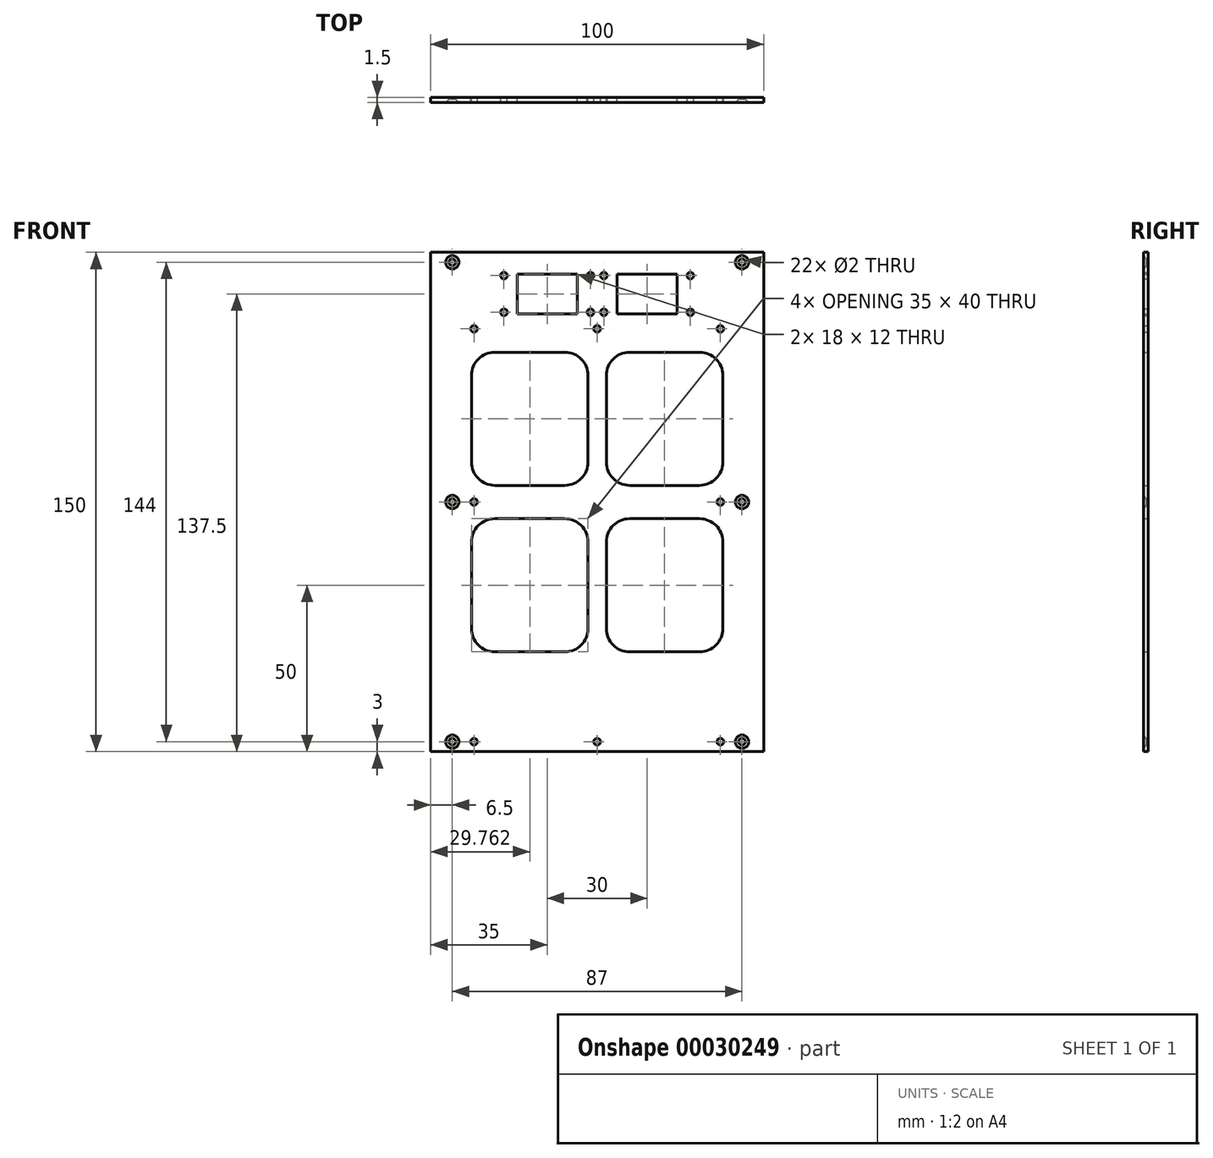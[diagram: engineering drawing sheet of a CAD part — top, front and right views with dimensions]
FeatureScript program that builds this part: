
annotation { "Feature Type Name" : "Feature", "Feature Type Description" : "" }
export const myFeature = defineFeature(function(context is Context, id is Id, definition is map)
    precondition{}
    {
        {
            var Q0;
            Q0=qCreatedBy(makeId("Front.planeOp"),FACE);
            var sketch = newSketch(context, id + "F0", { "sketchPlane" : qUnion([Q0])});
            skLineSegment(sketch, "E0.rect.bottom", {"start": v(-50, 75) * mm, "end": v(50, 75) * mm});
            skLineSegment(sketch, "E0.rect.top", {"start": v(-50, -75) * mm, "end": v(50, -75) * mm});
            skLineSegment(sketch, "E0.rect.left", {"start": v(-50, 75) * mm, "end": v(-50, -75) * mm});
            skLineSegment(sketch, "E0.rect.right", {"start": v(50, 75) * mm, "end": v(50, -75) * mm});
            skPoint(sketch, "E0.rect.middle", {"position": v(0, 0) * mm});
            skLineSegment(sketch, "E1.rect.bottom", {"start": v(-9.74, 5) * mm, "end": v(-30.74, 5) * mm});
            skLineSegment(sketch, "E1.rect.top", {"start": v(-9.74, 45) * mm, "end": v(-30.74, 45) * mm});
            skLineSegment(sketch, "E1.rect.left", {"start": v(-2.74, 12) * mm, "end": v(-2.74, 38) * mm});
            skLineSegment(sketch, "E1.rect.right", {"start": v(-37.74, 12) * mm, "end": v(-37.74, 38) * mm});
            skPoint(sketch, "E1.rect.middle", {"position": v(-20.24, 25) * mm});
            skPoint(sketch, "E2", {"position": v(0, 75) * mm});
            skPoint(sketch, "E3", {"position": v(-25, 75) * mm});
            skPoint(sketch, "E4.visualSharp", {"position": v(-2.74, 5) * mm});
            skArc(sketch, "E4.filletArc", {"start": v(-9.74, 5) * mm, "mid": v(-4.79, 7.05) * mm, "end": v(-2.74, 12) * mm});
            skPoint(sketch, "E5.visualSharp", {"position": v(-2.74, 45) * mm});
            skArc(sketch, "E5.filletArc", {"start": v(-2.74, 38) * mm, "mid": v(-4.79, 42.95) * mm, "end": v(-9.74, 45) * mm});
            skPoint(sketch, "E6.visualSharp", {"position": v(-37.74, 45) * mm});
            skArc(sketch, "E6.filletArc", {"start": v(-30.74, 45) * mm, "mid": v(-35.69, 42.95) * mm, "end": v(-37.74, 38) * mm});
            skPoint(sketch, "E7.visualSharp", {"position": v(-37.74, 5) * mm});
            skArc(sketch, "E7.filletArc", {"start": v(-37.74, 12) * mm, "mid": v(-35.69, 7.05) * mm, "end": v(-30.74, 5) * mm});
            skLineSegment(sketch, "E8.MirrorCS", {"start": v(2.74, 12) * mm, "end": v(2.74, 38) * mm});
            skArc(sketch, "E9.MirrorCS", {"start": v(2.74, 38) * mm, "mid": v(4.79, 42.95) * mm, "end": v(9.74, 45) * mm});
            skLineSegment(sketch, "E10.MirrorCS", {"start": v(9.74, 45) * mm, "end": v(30.74, 45) * mm});
            skPoint(sketch, "E11.MirrorP", {"position": v(37.74, 45) * mm});
            skArc(sketch, "E12.MirrorCS", {"start": v(30.74, 45) * mm, "mid": v(35.69, 42.95) * mm, "end": v(37.74, 38) * mm});
            skLineSegment(sketch, "E13.MirrorCS", {"start": v(37.74, 12) * mm, "end": v(37.74, 38) * mm});
            skPoint(sketch, "E14.MirrorP", {"position": v(37.74, 5) * mm});
            skLineSegment(sketch, "E15.MirrorCS", {"start": v(9.74, 5) * mm, "end": v(30.74, 5) * mm});
            skArc(sketch, "E16.MirrorCS", {"start": v(37.74, 12) * mm, "mid": v(35.69, 7.05) * mm, "end": v(30.74, 5) * mm});
            skPoint(sketch, "E17.MirrorP", {"position": v(2.74, 5) * mm});
            skArc(sketch, "E18.MirrorCS", {"start": v(9.74, 5) * mm, "mid": v(4.79, 7.05) * mm, "end": v(2.74, 12) * mm});
            skArc(sketch, "E19.MirrorCS", {"start": v(30.74, -45) * mm, "mid": v(35.69, -42.95) * mm, "end": v(37.74, -38) * mm});
            skArc(sketch, "E20.MirrorCS", {"start": v(37.74, -12) * mm, "mid": v(35.69, -7.05) * mm, "end": v(30.74, -5) * mm});
            skArc(sketch, "E21.MirrorCS", {"start": v(9.74, -5) * mm, "mid": v(4.79, -7.05) * mm, "end": v(2.74, -12) * mm});
            skArc(sketch, "E22.MirrorCS", {"start": v(2.74, -38) * mm, "mid": v(4.79, -42.95) * mm, "end": v(9.74, -45) * mm});
            skPoint(sketch, "E23.MirrorP", {"position": v(37.74, -45) * mm});
            skLineSegment(sketch, "E24.MirrorCS", {"start": v(37.74, -12) * mm, "end": v(37.74, -38) * mm});
            skPoint(sketch, "E25.MirrorP", {"position": v(37.74, -5) * mm});
            skLineSegment(sketch, "E26.MirrorCS", {"start": v(2.74, -12) * mm, "end": v(2.74, -38) * mm});
            skPoint(sketch, "E27.MirrorP", {"position": v(3.64, -53) * mm});
            skLineSegment(sketch, "E28.MirrorCS", {"start": v(9.74, -5) * mm, "end": v(30.74, -5) * mm});
            skLineSegment(sketch, "E29.MirrorCS", {"start": v(9.74, -45) * mm, "end": v(30.74, -45) * mm});
            skPoint(sketch, "E30.MirrorP", {"position": v(2.74, -5) * mm});
            skArc(sketch, "E31.MirrorCS", {"start": v(-9.74, -5) * mm, "mid": v(-4.79, -7.05) * mm, "end": v(-2.74, -12) * mm});
            skArc(sketch, "E32.MirrorCS", {"start": v(-2.74, -38) * mm, "mid": v(-4.79, -42.95) * mm, "end": v(-9.74, -45) * mm});
            skArc(sketch, "E33.MirrorCS", {"start": v(-37.74, -12) * mm, "mid": v(-35.69, -7.05) * mm, "end": v(-30.74, -5) * mm});
            skArc(sketch, "E34.MirrorCS", {"start": v(-30.74, -45) * mm, "mid": v(-35.69, -42.95) * mm, "end": v(-37.74, -38) * mm});
            skPoint(sketch, "E35.MirrorP", {"position": v(-20.24, -25) * mm});
            skPoint(sketch, "E36.MirrorP", {"position": v(-2.74, -5) * mm});
            skPoint(sketch, "E37.MirrorP", {"position": v(-37.74, -45) * mm});
            skLineSegment(sketch, "E38.MirrorCS", {"start": v(-9.74, -5) * mm, "end": v(-30.74, -5) * mm});
            skLineSegment(sketch, "E39.MirrorCS", {"start": v(-9.74, -45) * mm, "end": v(-30.74, -45) * mm});
            skPoint(sketch, "E40.MirrorP", {"position": v(-2.74, -45) * mm});
            skLineSegment(sketch, "E41.MirrorCS", {"start": v(-2.74, -12) * mm, "end": v(-2.74, -38) * mm});
            skLineSegment(sketch, "E42.MirrorCS", {"start": v(-37.74, -12) * mm, "end": v(-37.74, -38) * mm});
            skPoint(sketch, "E43.MirrorP", {"position": v(-37.74, -5) * mm});
            skLineSegment(sketch, "E44.bottom", {"start": v(-24, 68.5) * mm, "end": v(-6, 68.5) * mm});
            skLineSegment(sketch, "E44.top", {"start": v(-24, 56.5) * mm, "end": v(-6, 56.5) * mm});
            skLineSegment(sketch, "E44.left", {"start": v(-24, 68.5) * mm, "end": v(-24, 56.5) * mm});
            skLineSegment(sketch, "E44.right", {"start": v(-6, 68.5) * mm, "end": v(-6, 56.5) * mm});
            skPoint(sketch, "E45", {"position": v(-28, 57) * mm});
            skPoint(sketch, "E46", {"position": v(-28, 68) * mm});
            skPoint(sketch, "E47", {"position": v(-15, 68.5) * mm});
            skPoint(sketch, "E48", {"position": v(-15, 56.5) * mm});
            skLineSegment(sketch, "E49", {"start": v(-15, 68.5) * mm, "end": v(-15, 56.5) * mm});
            skPoint(sketch, "E50.MirrorP", {"position": v(-2, 68) * mm});
            skPoint(sketch, "E51.MirrorP", {"position": v(-2, 57) * mm});
            skPoint(sketch, "E52.MirrorP", {"position": v(2, 68) * mm});
            skPoint(sketch, "E53.MirrorP", {"position": v(28, 57) * mm});
            skPoint(sketch, "E54.MirrorP", {"position": v(2, 57) * mm});
            skLineSegment(sketch, "E55.MirrorCS", {"start": v(6, 68.5) * mm, "end": v(6, 56.5) * mm});
            skLineSegment(sketch, "E56.MirrorCS", {"start": v(24, 68.5) * mm, "end": v(6, 68.5) * mm});
            skLineSegment(sketch, "E57.MirrorCS", {"start": v(24, 68.5) * mm, "end": v(24, 56.5) * mm});
            skLineSegment(sketch, "E58.MirrorCS", {"start": v(15, 68.5) * mm, "end": v(15, 56.5) * mm});
            skPoint(sketch, "E59.MirrorP", {"position": v(15, 68.5) * mm});
            skPoint(sketch, "E60.MirrorP", {"position": v(28, 68) * mm});
            skLineSegment(sketch, "E61.MirrorCS", {"start": v(24, 56.5) * mm, "end": v(6, 56.5) * mm});
            skPoint(sketch, "E62.MirrorP", {"position": v(2.74, 45) * mm});
            skPoint(sketch, "E63.MirrorP", {"position": v(15, 56.5) * mm});
            skPoint(sketch, "E64", {"position": v(0, -75) * mm});
            skSolve(sketch);
        }
        {
            var Q0;
            Q0=makeQuery(id+"F0.imprint","IMPRINT",FACE,{"disambiguationData":[TD([[makeQuery(id+"F0.imprint","IMPRINT",EDGE,{"derivedFrom":sQuery(id+"F0.wireOp",EDGE,"E0.rect.bottom")}),-1.0]])]});
            extrude(context, id + "F1", {"entities" : qUnion([Q0]), "depth" : 1.5 * mm});
        }
        {
            var Q0;
            Q0=makeQuery(id+"F1.opExtrude","CAP_FACE",FACE,{"disambiguationData":[OSD([sQuery(id+"F0.wireOp",EDGE,"E0.rect.bottom"),sQuery(id+"F0.wireOp",EDGE,"E0.rect.top"),sQuery(id+"F0.wireOp",EDGE,"E0.rect.left"),sQuery(id+"F0.wireOp",EDGE,"E0.rect.right"),sQuery(id+"F0.wireOp",EDGE,"E1.rect.bottom"),sQuery(id+"F0.wireOp",EDGE,"E1.rect.top"),sQuery(id+"F0.wireOp",EDGE,"E1.rect.left"),sQuery(id+"F0.wireOp",EDGE,"E1.rect.right"),sQuery(id+"F0.wireOp",EDGE,"E4.filletArc"),sQuery(id+"F0.wireOp",EDGE,"E5.filletArc"),sQuery(id+"F0.wireOp",EDGE,"E6.filletArc"),sQuery(id+"F0.wireOp",EDGE,"E7.filletArc"),sQuery(id+"F0.wireOp",EDGE,"E8.MirrorCS"),sQuery(id+"F0.wireOp",EDGE,"E9.MirrorCS"),sQuery(id+"F0.wireOp",EDGE,"E10.MirrorCS"),sQuery(id+"F0.wireOp",EDGE,"E12.MirrorCS"),sQuery(id+"F0.wireOp",EDGE,"E13.MirrorCS"),sQuery(id+"F0.wireOp",EDGE,"E15.MirrorCS"),sQuery(id+"F0.wireOp",EDGE,"E16.MirrorCS"),sQuery(id+"F0.wireOp",EDGE,"E18.MirrorCS"),sQuery(id+"F0.wireOp",EDGE,"E19.MirrorCS"),sQuery(id+"F0.wireOp",EDGE,"E20.MirrorCS"),sQuery(id+"F0.wireOp",EDGE,"E21.MirrorCS"),sQuery(id+"F0.wireOp",EDGE,"E22.MirrorCS"),sQuery(id+"F0.wireOp",EDGE,"E24.MirrorCS"),sQuery(id+"F0.wireOp",EDGE,"E26.MirrorCS"),sQuery(id+"F0.wireOp",EDGE,"E28.MirrorCS"),sQuery(id+"F0.wireOp",EDGE,"E29.MirrorCS"),sQuery(id+"F0.wireOp",EDGE,"E31.MirrorCS"),sQuery(id+"F0.wireOp",EDGE,"E32.MirrorCS"),sQuery(id+"F0.wireOp",EDGE,"E33.MirrorCS"),sQuery(id+"F0.wireOp",EDGE,"E34.MirrorCS"),sQuery(id+"F0.wireOp",EDGE,"E38.MirrorCS"),sQuery(id+"F0.wireOp",EDGE,"E39.MirrorCS"),sQuery(id+"F0.wireOp",EDGE,"E41.MirrorCS"),sQuery(id+"F0.wireOp",EDGE,"E42.MirrorCS"),sQuery(id+"F0.wireOp",EDGE,"deea28ce-c4f6-4fc3-8f0f-82602a925565.rect.bottom"),sQuery(id+"F0.wireOp",EDGE,"deea28ce-c4f6-4fc3-8f0f-82602a925565.rect.top"),sQuery(id+"F0.wireOp",EDGE,"deea28ce-c4f6-4fc3-8f0f-82602a925565.rect.left"),sQuery(id+"F0.wireOp",EDGE,"deea28ce-c4f6-4fc3-8f0f-82602a925565.rect.right"),sQuery(id+"F0.wireOp",EDGE,"92293470-82ba-44ad-9286-e8a1911384cd.filletArc"),sQuery(id+"F0.wireOp",EDGE,"f783d059-47c1-4597-a3b5-ce5ed20d1783.filletArc"),sQuery(id+"F0.wireOp",EDGE,"7d8a2005-66fb-4448-9a0b-17e6f11710ed.filletArc"),sQuery(id+"F0.wireOp",EDGE,"bd1f88c4-01d0-4c1f-b818-689555ed0d3d.filletArc"),sQuery(id+"F0.wireOp",EDGE,"3de75153-5ae1-45d4-89d9-6fcf70203f930.MirrorCS"),sQuery(id+"F0.wireOp",EDGE,"3de75153-5ae1-45d4-89d9-6fcf70203f931.MirrorCS"),sQuery(id+"F0.wireOp",EDGE,"3de75153-5ae1-45d4-89d9-6fcf70203f932.MirrorCS"),sQuery(id+"F0.wireOp",EDGE,"3de75153-5ae1-45d4-89d9-6fcf70203f933.MirrorCS"),sQuery(id+"F0.wireOp",EDGE,"3de75153-5ae1-45d4-89d9-6fcf70203f937.MirrorCS"),sQuery(id+"F0.wireOp",EDGE,"3de75153-5ae1-45d4-89d9-6fcf70203f939.MirrorCS"),sQuery(id+"F0.wireOp",EDGE,"3de75153-5ae1-45d4-89d9-6fcf70203f9311.MirrorCS"),sQuery(id+"F0.wireOp",EDGE,"3de75153-5ae1-45d4-89d9-6fcf70203f9312.MirrorCS")])],"isStart":false});
            var sketch = newSketch(context, id + "F2", { "sketchPlane" : qUnion([Q0])});
            skPoint(sketch, "E65", {"position": v(-43.5, -72) * mm});
            skPoint(sketch, "E66.MirrorP", {"position": v(43.5, -72) * mm});
            skPoint(sketch, "E67.MirrorP", {"position": v(-43.5, 72) * mm});
            skPoint(sketch, "E68.MirrorP", {"position": v(43.5, 72) * mm});
            skPoint(sketch, "E69.MirrorP", {"position": v(-43.5, 0) * mm});
            skPoint(sketch, "E70.MirrorP", {"position": v(43.5, 0) * mm});
            skSolve(sketch);
        }
        {
            var Q0;
            Q0=sQuery(id+"F2.wireOp",VERTEX,"E65");
            var Q1;
            Q1=sQuery(id+"F2.wireOp",VERTEX,"E66.MirrorP");
            var Q2;
            Q2=sQuery(id+"F2.wireOp",VERTEX,"E68.MirrorP");
            var Q3;
            Q3=sQuery(id+"F2.wireOp",VERTEX,"E67.MirrorP");
            var Q4;
            Q4=sQuery(id+"F2.wireOp",VERTEX,"f692f96d-b3ef-4b25-bd05-95c4abe1053b");
            var Q5;
            Q5=sQuery(id+"F2.wireOp",VERTEX,"6fb1c37c-decf-44f5-8bba-7a2e60b1c09a");
            var Q6;
            Q6=sQuery(id+"F2.wireOp",VERTEX,"e5432b45-bd6c-42e0-96c4-d4a1cdefc3be");
            var Q7;
            Q7=sQuery(id+"F2.wireOp",VERTEX,"cf76a1ca-a373-4096-b586-4708a9325641");
            var Q8;
            Q8=sQuery(id+"F2.wireOp",VERTEX,"19e9ac87-c4db-4f84-8793-d0dcfe6b89480.MirrorP");
            var Q9;
            Q9=sQuery(id+"F2.wireOp",VERTEX,"cf40c92d-3cb4-4fd1-9011-2b1b11cf86800.MirrorP");
            var Q10;
            Q10=sQuery(id+"F2.wireOp",VERTEX,"dbe2afd2-cc13-4726-9d4e-a7426feb8f1a0.MirrorP");
            var Q11;
            Q11=sQuery(id+"F2.wireOp",VERTEX,"da7565b5-0760-4871-9ab9-0602c46f39720.MirrorP");
            var Q12;
            Q12=sQuery(id+"F2.wireOp",VERTEX,"17fecccd-3962-452f-9978-7328e825eee30.MirrorP");
            var Q13;
            Q13=sQuery(id+"F2.wireOp",VERTEX,"4bd07c42-14cb-4c0a-9484-79320a5c3db60.MirrorP");
            var Q14;
            Q14=sQuery(id+"F2.wireOp",VERTEX,"4bebc43e-6cee-4dba-a944-25e79cf908630.MirrorP");
            var Q15;
            Q15=sQuery(id+"F2.wireOp",VERTEX,"e56d2771-9223-44ee-8796-3a5c91e851be0.MirrorP");
            var Q16;
            Q16=sQuery(id+"F2.wireOp",VERTEX,"fc323023-5ca8-47af-bc60-2d4e8e6fe2a30.MirrorP");
            var Q17;
            Q17=sQuery(id+"F2.wireOp",VERTEX,"0839c29d-2d7f-409f-b01c-e3268e62f07b0.MirrorP");
            var Q18;
            Q18=sQuery(id+"F2.wireOp",VERTEX,"a23aa490-2248-47f4-872f-093390e742580.MirrorP");
            var Q19;
            Q19=sQuery(id+"F2.wireOp",VERTEX,"f29489ae-a8f8-488d-b8ee-71de4e1048c30.MirrorP");
            var Q20;
            Q20=sQuery(id+"F2.wireOp",VERTEX,"E69.MirrorP");
            var Q21;
            Q21=sQuery(id+"F2.wireOp",VERTEX,"E70.MirrorP");
            var Q22;
            Q22=makeQuery(id+"F1.opExtrude","SWEPT_BODY",BODY,{"disambiguationData":[OSD([sQuery(id+"F0.wireOp",EDGE,"E0.rect.bottom"),sQuery(id+"F0.wireOp",EDGE,"E0.rect.top"),sQuery(id+"F0.wireOp",EDGE,"E0.rect.left"),sQuery(id+"F0.wireOp",EDGE,"E0.rect.right"),sQuery(id+"F0.wireOp",EDGE,"E1.rect.bottom"),sQuery(id+"F0.wireOp",EDGE,"E1.rect.top"),sQuery(id+"F0.wireOp",EDGE,"E1.rect.left"),sQuery(id+"F0.wireOp",EDGE,"E1.rect.right"),sQuery(id+"F0.wireOp",EDGE,"E4.filletArc"),sQuery(id+"F0.wireOp",EDGE,"E5.filletArc"),sQuery(id+"F0.wireOp",EDGE,"E6.filletArc"),sQuery(id+"F0.wireOp",EDGE,"E7.filletArc"),sQuery(id+"F0.wireOp",EDGE,"E8.MirrorCS"),sQuery(id+"F0.wireOp",EDGE,"E9.MirrorCS"),sQuery(id+"F0.wireOp",EDGE,"E10.MirrorCS"),sQuery(id+"F0.wireOp",EDGE,"E12.MirrorCS"),sQuery(id+"F0.wireOp",EDGE,"E13.MirrorCS"),sQuery(id+"F0.wireOp",EDGE,"E15.MirrorCS"),sQuery(id+"F0.wireOp",EDGE,"E16.MirrorCS"),sQuery(id+"F0.wireOp",EDGE,"E18.MirrorCS"),sQuery(id+"F0.wireOp",EDGE,"E19.MirrorCS"),sQuery(id+"F0.wireOp",EDGE,"E20.MirrorCS"),sQuery(id+"F0.wireOp",EDGE,"E21.MirrorCS"),sQuery(id+"F0.wireOp",EDGE,"E22.MirrorCS"),sQuery(id+"F0.wireOp",EDGE,"E24.MirrorCS"),sQuery(id+"F0.wireOp",EDGE,"E26.MirrorCS"),sQuery(id+"F0.wireOp",EDGE,"E28.MirrorCS"),sQuery(id+"F0.wireOp",EDGE,"E29.MirrorCS"),sQuery(id+"F0.wireOp",EDGE,"E31.MirrorCS"),sQuery(id+"F0.wireOp",EDGE,"E32.MirrorCS"),sQuery(id+"F0.wireOp",EDGE,"E33.MirrorCS"),sQuery(id+"F0.wireOp",EDGE,"E34.MirrorCS"),sQuery(id+"F0.wireOp",EDGE,"E38.MirrorCS"),sQuery(id+"F0.wireOp",EDGE,"E39.MirrorCS"),sQuery(id+"F0.wireOp",EDGE,"E41.MirrorCS"),sQuery(id+"F0.wireOp",EDGE,"E42.MirrorCS"),sQuery(id+"F0.wireOp",EDGE,"deea28ce-c4f6-4fc3-8f0f-82602a925565.rect.bottom"),sQuery(id+"F0.wireOp",EDGE,"deea28ce-c4f6-4fc3-8f0f-82602a925565.rect.top"),sQuery(id+"F0.wireOp",EDGE,"deea28ce-c4f6-4fc3-8f0f-82602a925565.rect.left"),sQuery(id+"F0.wireOp",EDGE,"deea28ce-c4f6-4fc3-8f0f-82602a925565.rect.right"),sQuery(id+"F0.wireOp",EDGE,"92293470-82ba-44ad-9286-e8a1911384cd.filletArc"),sQuery(id+"F0.wireOp",EDGE,"f783d059-47c1-4597-a3b5-ce5ed20d1783.filletArc"),sQuery(id+"F0.wireOp",EDGE,"7d8a2005-66fb-4448-9a0b-17e6f11710ed.filletArc"),sQuery(id+"F0.wireOp",EDGE,"bd1f88c4-01d0-4c1f-b818-689555ed0d3d.filletArc"),sQuery(id+"F0.wireOp",EDGE,"3de75153-5ae1-45d4-89d9-6fcf70203f930.MirrorCS"),sQuery(id+"F0.wireOp",EDGE,"3de75153-5ae1-45d4-89d9-6fcf70203f931.MirrorCS"),sQuery(id+"F0.wireOp",EDGE,"3de75153-5ae1-45d4-89d9-6fcf70203f932.MirrorCS"),sQuery(id+"F0.wireOp",EDGE,"3de75153-5ae1-45d4-89d9-6fcf70203f933.MirrorCS"),sQuery(id+"F0.wireOp",EDGE,"3de75153-5ae1-45d4-89d9-6fcf70203f937.MirrorCS"),sQuery(id+"F0.wireOp",EDGE,"3de75153-5ae1-45d4-89d9-6fcf70203f939.MirrorCS"),sQuery(id+"F0.wireOp",EDGE,"3de75153-5ae1-45d4-89d9-6fcf70203f9311.MirrorCS"),sQuery(id+"F0.wireOp",EDGE,"3de75153-5ae1-45d4-89d9-6fcf70203f9312.MirrorCS")])]});
            hole(context, id + "F3", {"style" : HoleStyle.C_SINK, "holeDiameter" : 2 * mm, "cSinkDiameter" : 4 * mm, "endStyle" : HoleEndStyle.THROUGH, "locations" : qUnion([Q0, Q1, Q2, Q3, Q4, Q5, Q6, Q7, Q8, Q9, Q10, Q11, Q12, Q13, Q14, Q15, Q16, Q17, Q18, Q19, Q20, Q21]), "scope" : qUnion([Q22]), "cSinkAngle" : 90 * degree, "isTappedThrough" : true});
        }
        {
            var Q0;
            Q0=sQuery(id+"F0.wireOp",VERTEX,"E46");
            var Q1;
            Q1=sQuery(id+"F0.wireOp",VERTEX,"E45");
            var Q2;
            Q2=sQuery(id+"F0.wireOp",VERTEX,"E51.MirrorP");
            var Q3;
            Q3=sQuery(id+"F0.wireOp",VERTEX,"E50.MirrorP");
            var Q4;
            Q4=sQuery(id+"F0.wireOp",VERTEX,"E52.MirrorP");
            var Q5;
            Q5=sQuery(id+"F0.wireOp",VERTEX,"E54.MirrorP");
            var Q6;
            Q6=sQuery(id+"F0.wireOp",VERTEX,"E53.MirrorP");
            var Q7;
            Q7=sQuery(id+"F0.wireOp",VERTEX,"E60.MirrorP");
            var Q8;
            Q8=makeQuery(id+"F1.opExtrude","SWEPT_BODY",BODY,{"disambiguationData":[OSD([sQuery(id+"F0.wireOp",EDGE,"E0.rect.bottom"),sQuery(id+"F0.wireOp",EDGE,"E0.rect.top"),sQuery(id+"F0.wireOp",EDGE,"E0.rect.left"),sQuery(id+"F0.wireOp",EDGE,"E0.rect.right"),sQuery(id+"F0.wireOp",EDGE,"E1.rect.bottom"),sQuery(id+"F0.wireOp",EDGE,"E1.rect.top"),sQuery(id+"F0.wireOp",EDGE,"E1.rect.left"),sQuery(id+"F0.wireOp",EDGE,"E1.rect.right"),sQuery(id+"F0.wireOp",EDGE,"E4.filletArc"),sQuery(id+"F0.wireOp",EDGE,"E5.filletArc"),sQuery(id+"F0.wireOp",EDGE,"E6.filletArc"),sQuery(id+"F0.wireOp",EDGE,"E7.filletArc"),sQuery(id+"F0.wireOp",EDGE,"E8.MirrorCS"),sQuery(id+"F0.wireOp",EDGE,"E9.MirrorCS"),sQuery(id+"F0.wireOp",EDGE,"E10.MirrorCS"),sQuery(id+"F0.wireOp",EDGE,"E12.MirrorCS"),sQuery(id+"F0.wireOp",EDGE,"E13.MirrorCS"),sQuery(id+"F0.wireOp",EDGE,"E15.MirrorCS"),sQuery(id+"F0.wireOp",EDGE,"E16.MirrorCS"),sQuery(id+"F0.wireOp",EDGE,"E18.MirrorCS"),sQuery(id+"F0.wireOp",EDGE,"E19.MirrorCS"),sQuery(id+"F0.wireOp",EDGE,"E20.MirrorCS"),sQuery(id+"F0.wireOp",EDGE,"E21.MirrorCS"),sQuery(id+"F0.wireOp",EDGE,"E22.MirrorCS"),sQuery(id+"F0.wireOp",EDGE,"E24.MirrorCS"),sQuery(id+"F0.wireOp",EDGE,"E26.MirrorCS"),sQuery(id+"F0.wireOp",EDGE,"E28.MirrorCS"),sQuery(id+"F0.wireOp",EDGE,"E29.MirrorCS"),sQuery(id+"F0.wireOp",EDGE,"E31.MirrorCS"),sQuery(id+"F0.wireOp",EDGE,"E32.MirrorCS"),sQuery(id+"F0.wireOp",EDGE,"E33.MirrorCS"),sQuery(id+"F0.wireOp",EDGE,"E34.MirrorCS"),sQuery(id+"F0.wireOp",EDGE,"E38.MirrorCS"),sQuery(id+"F0.wireOp",EDGE,"E39.MirrorCS"),sQuery(id+"F0.wireOp",EDGE,"E41.MirrorCS"),sQuery(id+"F0.wireOp",EDGE,"E42.MirrorCS"),sQuery(id+"F0.wireOp",EDGE,"0ad36b47-e3a2-4d15-89b1-ac590451d19c"),sQuery(id+"F0.wireOp",EDGE,"E44.bottom"),sQuery(id+"F0.wireOp",EDGE,"E44.top"),sQuery(id+"F0.wireOp",EDGE,"E44.left"),sQuery(id+"F0.wireOp",EDGE,"E44.right"),sQuery(id+"F0.wireOp",EDGE,"E55.MirrorCS"),sQuery(id+"F0.wireOp",EDGE,"E56.MirrorCS"),sQuery(id+"F0.wireOp",EDGE,"E57.MirrorCS"),sQuery(id+"F0.wireOp",EDGE,"E61.MirrorCS")])]});
            hole(context, id + "F4", {"style" : HoleStyle.SIMPLE, "endStyle" : HoleEndStyle.THROUGH, "oppositeDirection" : true, "holeDiameter" : 2 * mm, "locations" : qUnion([Q0, Q1, Q2, Q3, Q4, Q5, Q6, Q7]), "scope" : qUnion([Q8]), "isTappedThrough" : true});
        }
        {
            var Q0;
            Q0=qCreatedBy(makeId("Front.planeOp"),FACE);
            var sketch = newSketch(context, id + "F5", { "sketchPlane" : qUnion([Q0])});
            skCircle(sketch, "E71", {"center": v(-37, -72) * mm, "radius": 1 * mm});
            skCircle(sketch, "E72.0.1.0", {"center": v(-37, 52) * mm, "radius": 1 * mm});
            skCircle(sketch, "E72.1.0.0", {"center": v(0, -72) * mm, "radius": 1 * mm});
            skCircle(sketch, "E72.1.1.0", {"center": v(0, 52) * mm, "radius": 1 * mm});
            skCircle(sketch, "E72.2.0.0", {"center": v(37, -72) * mm, "radius": 1 * mm});
            skCircle(sketch, "E72.2.1.0", {"center": v(37, 52) * mm, "radius": 1 * mm});
            skLineSegment(sketch, "E72.direction1", {"start": v(-37, -72) * mm, "end": v(0, -72) * mm, "construction": true});
            skLineSegment(sketch, "E72.direction2", {"start": v(-37, -72) * mm, "end": v(-37, 52) * mm, "construction": true});
            skPoint(sketch, "E73", {"position": v(-37, 0) * mm});
            skPoint(sketch, "E74.MirrorP", {"position": v(37, 0) * mm});
            skSolve(sketch);
        }
        {
            var Q0;
            Q0=sQuery(id+"F5.wireOp",VERTEX,"E72.direction1.start");
            var Q1;
            Q1=sQuery(id+"F5.wireOp",VERTEX,"E72.direction1.end");
            var Q2;
            Q2=sQuery(id+"F5.wireOp",VERTEX,"E72.2.0.0.center");
            var Q3;
            Q3=sQuery(id+"F5.wireOp",VERTEX,"E72.1.1.0.center");
            var Q4;
            Q4=sQuery(id+"F5.wireOp",VERTEX,"E72.1.2.0.center");
            var Q5;
            Q5=sQuery(id+"F5.wireOp",VERTEX,"E72.2.2.0.center");
            var Q6;
            Q6=sQuery(id+"F5.wireOp",VERTEX,"E72.0.2.0.center");
            var Q7;
            Q7=sQuery(id+"F5.wireOp",VERTEX,"E72.direction2.end");
            var Q8;
            Q8=sQuery(id+"F5.wireOp",VERTEX,"E72.2.1.0.center");
            var Q9;
            Q9=sQuery(id+"F5.wireOp",VERTEX,"8d9ffd20-42a7-48bb-b160-9022e51994f8");
            var Q10;
            Q10=sQuery(id+"F5.wireOp",VERTEX,"2204d435-fe16-46ed-8ace-113c7e8db4ec0.MirrorP");
            var Q11;
            Q11=sQuery(id+"F5.wireOp",VERTEX,"E73");
            var Q12;
            Q12=sQuery(id+"F5.wireOp",VERTEX,"E74.MirrorP");
            var Q13;
            Q13=makeQuery(id+"F1.opExtrude","SWEPT_BODY",BODY,{"disambiguationData":[OSD([sQuery(id+"F0.wireOp",EDGE,"E0.rect.bottom"),sQuery(id+"F0.wireOp",EDGE,"E0.rect.top"),sQuery(id+"F0.wireOp",EDGE,"E0.rect.left"),sQuery(id+"F0.wireOp",EDGE,"E0.rect.right"),sQuery(id+"F0.wireOp",EDGE,"E1.rect.bottom"),sQuery(id+"F0.wireOp",EDGE,"E1.rect.top"),sQuery(id+"F0.wireOp",EDGE,"E1.rect.left"),sQuery(id+"F0.wireOp",EDGE,"E1.rect.right"),sQuery(id+"F0.wireOp",EDGE,"E4.filletArc"),sQuery(id+"F0.wireOp",EDGE,"E5.filletArc"),sQuery(id+"F0.wireOp",EDGE,"E6.filletArc"),sQuery(id+"F0.wireOp",EDGE,"E7.filletArc"),sQuery(id+"F0.wireOp",EDGE,"E8.MirrorCS"),sQuery(id+"F0.wireOp",EDGE,"E9.MirrorCS"),sQuery(id+"F0.wireOp",EDGE,"E10.MirrorCS"),sQuery(id+"F0.wireOp",EDGE,"E12.MirrorCS"),sQuery(id+"F0.wireOp",EDGE,"E13.MirrorCS"),sQuery(id+"F0.wireOp",EDGE,"E15.MirrorCS"),sQuery(id+"F0.wireOp",EDGE,"E16.MirrorCS"),sQuery(id+"F0.wireOp",EDGE,"E18.MirrorCS"),sQuery(id+"F0.wireOp",EDGE,"E19.MirrorCS"),sQuery(id+"F0.wireOp",EDGE,"E20.MirrorCS"),sQuery(id+"F0.wireOp",EDGE,"E21.MirrorCS"),sQuery(id+"F0.wireOp",EDGE,"E22.MirrorCS"),sQuery(id+"F0.wireOp",EDGE,"E24.MirrorCS"),sQuery(id+"F0.wireOp",EDGE,"E26.MirrorCS"),sQuery(id+"F0.wireOp",EDGE,"E28.MirrorCS"),sQuery(id+"F0.wireOp",EDGE,"E29.MirrorCS"),sQuery(id+"F0.wireOp",EDGE,"E31.MirrorCS"),sQuery(id+"F0.wireOp",EDGE,"E32.MirrorCS"),sQuery(id+"F0.wireOp",EDGE,"E33.MirrorCS"),sQuery(id+"F0.wireOp",EDGE,"E34.MirrorCS"),sQuery(id+"F0.wireOp",EDGE,"E38.MirrorCS"),sQuery(id+"F0.wireOp",EDGE,"E39.MirrorCS"),sQuery(id+"F0.wireOp",EDGE,"E41.MirrorCS"),sQuery(id+"F0.wireOp",EDGE,"E42.MirrorCS"),sQuery(id+"F0.wireOp",EDGE,"0ad36b47-e3a2-4d15-89b1-ac590451d19c"),sQuery(id+"F0.wireOp",EDGE,"E44.bottom"),sQuery(id+"F0.wireOp",EDGE,"E44.top"),sQuery(id+"F0.wireOp",EDGE,"E44.left"),sQuery(id+"F0.wireOp",EDGE,"E44.right"),sQuery(id+"F0.wireOp",EDGE,"E55.MirrorCS"),sQuery(id+"F0.wireOp",EDGE,"E56.MirrorCS"),sQuery(id+"F0.wireOp",EDGE,"E57.MirrorCS"),sQuery(id+"F0.wireOp",EDGE,"E61.MirrorCS")])]});
            hole(context, id + "F6", {"style" : HoleStyle.SIMPLE, "endStyle" : HoleEndStyle.THROUGH, "oppositeDirection" : true, "holeDiameter" : 2 * mm, "locations" : qUnion([Q0, Q1, Q2, Q3, Q4, Q5, Q6, Q7, Q8, Q9, Q10, Q11, Q12]), "scope" : qUnion([Q13]), "isTappedThrough" : true});
        }
    });
